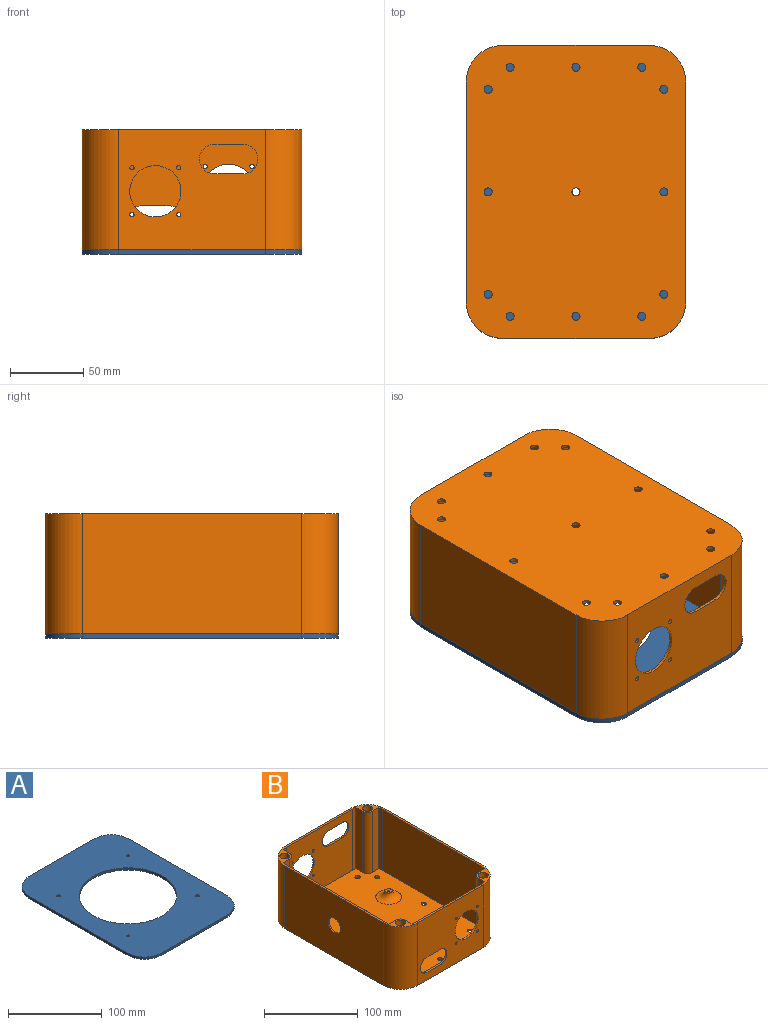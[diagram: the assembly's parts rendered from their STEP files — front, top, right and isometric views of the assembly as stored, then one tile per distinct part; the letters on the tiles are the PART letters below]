
ASSEMBLY  parts=2 mates=1
PART A: 15 faces, bbox 150x200x3 mm
  f0: plane 150x3mm, normal (-1,0,0), area 450mm2, adj f1,f7,f8,f9
  f1: cylinder r=25mm len=25mm, axis (0,0,-1), area 117.8mm2, adj f0,f2,f8,f9
  f2: plane 100x3mm, normal (0,-1,0), area 300mm2, adj f1,f3,f8,f9
  f3: cylinder r=25mm len=25mm, axis (0,0,-1), area 117.8mm2, adj f2,f4,f8,f9
  f4: plane 150x3mm, normal (1,0,0), area 450mm2, adj f3,f5,f8,f9
  f5: cylinder r=25mm len=25mm, axis (0,0,-1), area 117.8mm2, adj f4,f6,f8,f9
  f6: plane 100x3mm, normal (0,1,0), area 300mm2, adj f5,f7,f8,f9
  f7: cylinder r=25mm len=25mm, axis (0,0,-1), area 117.8mm2, adj f0,f6,f8,f9
  f8: plane 200x150mm, normal (0,0,1), area 20930.1mm2, adj f0,f1,f2,f3,f4,f5,f6,f7
  f9: plane 200x150mm, normal (0,0,-1), area 20930.1mm2, adj f0,f1,f2,f3,f4,f5,f6,f7
  f10: cylinder r=1.75mm len=3.5mm, axis (0,0,1), area 33mm2, adj f8,f9
  f11: cylinder r=1.75mm len=3.5mm, axis (0,0,1), area 33mm2, adj f8,f9
  f12: cylinder r=52mm len=104mm, axis (0,0,1), area 980.2mm2, adj f8,f9
  f13: cylinder r=1.75mm len=3.5mm, axis (0,0,1), area 33mm2, adj f8,f9
  f14: cylinder r=1.75mm len=3.5mm, axis (0,0,1), area 33mm2, adj f8,f9
PART B: 95 faces, bbox 150x200x82 mm
  f0: cylinder r=23mm len=80mm, axis (0,0,-1), area 407.4mm2, adj f4,f13,f16,f31
  f1: cylinder r=23mm len=80mm, axis (0,0,-1), area 407.4mm2, adj f4,f13,f14,f33
  f2: cylinder r=23mm len=80mm, axis (0,0,-1), area 407.4mm2, adj f4,f13,f17,f24
  f3: cylinder r=23mm len=80mm, axis (0,0,-1), area 407.4mm2, adj f4,f13,f15,f27
  f4: plane 196x146mm, normal (0,0,1), area 24068.7mm2, adj f0,f1,f2,f3,f5,f6,f7,f8
  f5: cylinder r=23mm len=80mm, axis (0,0,-1), area 407.4mm2, adj f4,f13,f14,f29
  f6: cylinder r=23mm len=80mm, axis (0,0,-1), area 407.4mm2, adj f4,f13,f15,f32
  f7: cylinder r=23mm len=80mm, axis (0,0,-1), area 407.4mm2, adj f4,f13,f16,f23
  f8: cylinder r=23mm len=80mm, axis (0,0,-1), area 407.4mm2, adj f4,f13,f17,f26
  f9: plane 100x82mm, normal (0,-1,0), area 6497.3mm2, adj f13,f18,f21,f22,f65,f66,f67,f68
  f10: plane 150x82mm, normal (1,0,0), area 12300mm2, adj f13,f18,f19,f22
  f11: plane 100x82mm, normal (0,1,0), area 6497.3mm2, adj f13,f18,f19,f20,f56,f57,f58,f59
  f12: plane 150x82mm, normal (-1,0,0), area 12013.5mm2, adj f13,f18,f20,f21,f74
  f13: plane 200x150mm, normal (0,0,1), area 1749mm2, adj f0,f1,f2,f3,f5,f6,f7,f8
  f14: plane 100x80mm, normal (0,1,0), area 6297.3mm2, adj f1,f4,f5,f13,f65,f66,f67,f68
  f15: plane 150x80mm, normal (-1,0,0), area 12000mm2, adj f3,f4,f6,f13
  f16: plane 150x80mm, normal (1,0,0), area 11713.5mm2, adj f0,f4,f7,f13,f74
  f17: plane 100x80mm, normal (0,-1,0), area 6297.3mm2, adj f2,f4,f8,f13,f56,f57,f58,f59
  f18: plane 200x150mm, normal (0,0,-1), area 29154.6mm2, adj f9,f10,f11,f12,f19,f20,f21,f22
  f19: cylinder r=25mm len=82mm, axis (0,0,-1), area 3220.1mm2, adj f10,f11,f13,f18
  f20: cylinder r=25mm len=82mm, axis (0,0,-1), area 3220.1mm2, adj f11,f12,f13,f18
  f21: cylinder r=25mm len=82mm, axis (0,0,-1), area 3220.1mm2, adj f9,f12,f13,f18
  f22: cylinder r=25mm len=82mm, axis (0,0,-1), area 3220.1mm2, adj f9,f10,f13,f18
  f23: plane 80x9.89mm, normal (0,-1,0), area 791mm2, adj f4,f7,f13,f39
  f24: plane 80x9.89mm, normal (1,0,0), area 791mm2, adj f2,f4,f13,f39
  f25: cylinder r=5.25mm len=10.5mm, axis (0,0,1), area 329.9mm2, adj f13,f36
  f26: plane 80x9.89mm, normal (-1,0,0), area 791mm2, adj f4,f8,f13,f40
  f27: plane 80x9.89mm, normal (0,-1,0), area 791mm2, adj f3,f4,f13,f40
  f28: cylinder r=5.25mm len=10.5mm, axis (0,0,1), area 329.9mm2, adj f13,f35
  f29: plane 80x9.89mm, normal (1,0,0), area 791mm2, adj f4,f5,f13,f42
  f30: cylinder r=5.25mm len=10.5mm, axis (0,0,1), area 329.9mm2, adj f13,f38
  f31: plane 80x9.89mm, normal (0,1,0), area 791mm2, adj f0,f4,f13,f42
  f32: plane 80x9.89mm, normal (0,1,0), area 791mm2, adj f4,f6,f13,f41
  f33: plane 80x9.89mm, normal (-1,0,0), area 791mm2, adj f1,f4,f13,f41
  f34: cylinder r=5.25mm len=10.5mm, axis (0,0,1), area 329.9mm2, adj f13,f37
  f35: plane 10.5x10.5mm, normal (0,0,1), area 86.6mm2, adj f28
  f36: plane 10.5x10.5mm, normal (0,0,1), area 86.6mm2, adj f25
  f37: plane 10.5x10.5mm, normal (0,0,1), area 86.6mm2, adj f34
  f38: plane 10.5x10.5mm, normal (0,0,1), area 86.6mm2, adj f30
  f39: cylinder r=7.5mm len=80mm, axis (0,0,-1), area 942.5mm2, adj f4,f13,f23,f24
  f40: cylinder r=7.5mm len=80mm, axis (0,0,1), area 942.5mm2, adj f4,f13,f26,f27
  f41: cylinder r=7.5mm len=80mm, axis (0,0,1), area 942.5mm2, adj f4,f13,f32,f33
  f42: cylinder r=7.5mm len=80mm, axis (0,0,1), area 942.5mm2, adj f4,f13,f29,f31
  f43: cylinder r=2.75mm len=5.5mm, axis (0,0,-1), area 34.6mm2, adj f4,f18
  f44: cylinder r=2.75mm len=5.5mm, axis (0,0,-1), area 34.6mm2, adj f4,f18
  f45: cylinder r=2.75mm len=5.5mm, axis (0,0,-1), area 34.6mm2, adj f4,f18
  f46: cylinder r=2.75mm len=5.5mm, axis (0,0,-1), area 34.6mm2, adj f4,f18
  f47: cylinder r=2.75mm len=5.5mm, axis (0,0,-1), area 34.6mm2, adj f4,f18
  f48: cylinder r=2.75mm len=5.5mm, axis (0,0,-1), area 34.6mm2, adj f4,f18,f83
  f49: cylinder r=2.75mm len=5.5mm, axis (0,0,-1), area 34.6mm2, adj f4,f18
  f50: cylinder r=2.75mm len=5.5mm, axis (0,0,-1), area 34.6mm2, adj f4,f18
  f51: cylinder r=2.75mm len=5.5mm, axis (0,0,-1), area 34.6mm2, adj f4,f18
  f52: cylinder r=2.75mm len=5.5mm, axis (0,0,-1), area 34.6mm2, adj f4,f18
  f53: cylinder r=2.75mm len=5.5mm, axis (0,0,-1), area 34.6mm2, adj f4,f18
  f54: cylinder r=2.75mm len=5.5mm, axis (0,0,-1), area 34.6mm2, adj f4,f18
  f55: cylinder r=2.75mm len=5.5mm, axis (0,0,-1), area 34.6mm2, adj f4,f18
  f56: cylinder r=10mm len=20mm, axis (0,1,0), area 62.8mm2, adj f11,f17,f57,f59
  f57: plane 20x2mm, normal (0,0,-1), area 40mm2, adj f11,f17,f56,f58
  f58: cylinder r=10mm len=20mm, axis (0,1,0), area 62.8mm2, adj f11,f17,f57,f59
  f59: plane 20x2mm, normal (0,0,1), area 40mm2, adj f11,f17,f56,f58
  f60: cylinder r=1.45mm len=2.9mm, axis (0,1,0), area 18.2mm2, adj f11,f17
  f61: cylinder r=1.45mm len=2.9mm, axis (0,1,0), area 18.2mm2, adj f11,f17
  f62: cylinder r=17.5mm len=35mm, axis (0,1,0), area 219.9mm2, adj f11,f17
  f63: cylinder r=1.45mm len=2.9mm, axis (0,1,0), area 18.2mm2, adj f11,f17
  f64: cylinder r=1.45mm len=2.9mm, axis (0,1,0), area 18.2mm2, adj f11,f17
  f65: cylinder r=10mm len=20mm, axis (0,-1,0), area 62.8mm2, adj f9,f14,f66,f68
  f66: plane 20x2mm, normal (0,0,1), area 40mm2, adj f9,f14,f65,f67
  f67: cylinder r=10mm len=20mm, axis (0,-1,0), area 62.8mm2, adj f9,f14,f66,f68
  f68: plane 20x2mm, normal (0,0,-1), area 40mm2, adj f9,f14,f65,f67
  f69: cylinder r=17.5mm len=35mm, axis (0,-1,0), area 219.9mm2, adj f9,f14
  f70: cylinder r=1.45mm len=2.9mm, axis (0,-1,0), area 18.2mm2, adj f9,f14
  f71: cylinder r=1.45mm len=2.9mm, axis (0,-1,0), area 18.2mm2, adj f9,f14
  f72: cylinder r=1.45mm len=2.9mm, axis (0,-1,0), area 18.2mm2, adj f9,f14
  f73: cylinder r=1.45mm len=2.9mm, axis (0,-1,0), area 18.2mm2, adj f9,f14
  f74: cylinder r=9.55mm len=19.1mm, axis (-1,0,0), area 120mm2, adj f12,f16
  f75: plane 8x8mm, normal (0,0,1), area 44.1mm2, adj f84,f93
  f76: plane 8x8mm, normal (0,0,1), area 44.1mm2, adj f83,f91
  f77: plane 8x8mm, normal (0,0,1), area 44.1mm2, adj f82,f89
  f78: plane 8x8mm, normal (0,0,1), area 44.1mm2, adj f81,f87
  f79: plane 8x8mm, normal (0,0,1), area 44.1mm2, adj f80,f85
  f80: torus R=13.8mm, axis (0,0,1), area 684.6mm2, adj f4,f79
  f81: torus R=13.8mm, axis (0,0,1), area 684.6mm2, adj f4,f78
  f82: torus R=13.8mm, axis (0,0,1), area 684.6mm2, adj f4,f77
  f83: torus R=13.8mm, axis (0,0,1), area 684.6mm2, adj f4,f48,f76
  f84: torus R=13.8mm, axis (0,0,1), area 684.6mm2, adj f4,f75
  f85: cylinder r=1.4mm len=7mm, axis (0,0,1), area 61.6mm2, adj f79,f86
  f86: plane 2.8x2.8mm, normal (0,0,1), area 6.2mm2, adj f85
  f87: cylinder r=1.4mm len=7mm, axis (0,0,1), area 61.6mm2, adj f78,f88
  f88: plane 2.8x2.8mm, normal (0,0,1), area 6.2mm2, adj f87
  f89: cylinder r=1.4mm len=7mm, axis (0,0,1), area 61.6mm2, adj f77,f90
  f90: plane 2.8x2.8mm, normal (0,0,1), area 6.2mm2, adj f89
  f91: cylinder r=1.4mm len=7mm, axis (0,0,1), area 61.6mm2, adj f76,f92
  f92: plane 2.8x2.8mm, normal (0,0,1), area 6.2mm2, adj f91
  f93: cylinder r=1.4mm len=7mm, axis (0,0,1), area 61.6mm2, adj f75,f94
  f94: plane 2.8x2.8mm, normal (0,0,1), area 6.2mm2, adj f93
PLACE A t=(118.57,87.54,27.12)mm
PLACE B rot(axis=(0,1,0),180deg) t=(118.57,87.54,112.12)mm
MATE fastened B.f13 <-> A.f8  axis (0,0,-1) through (118.57,-12.46,30.12)mm
